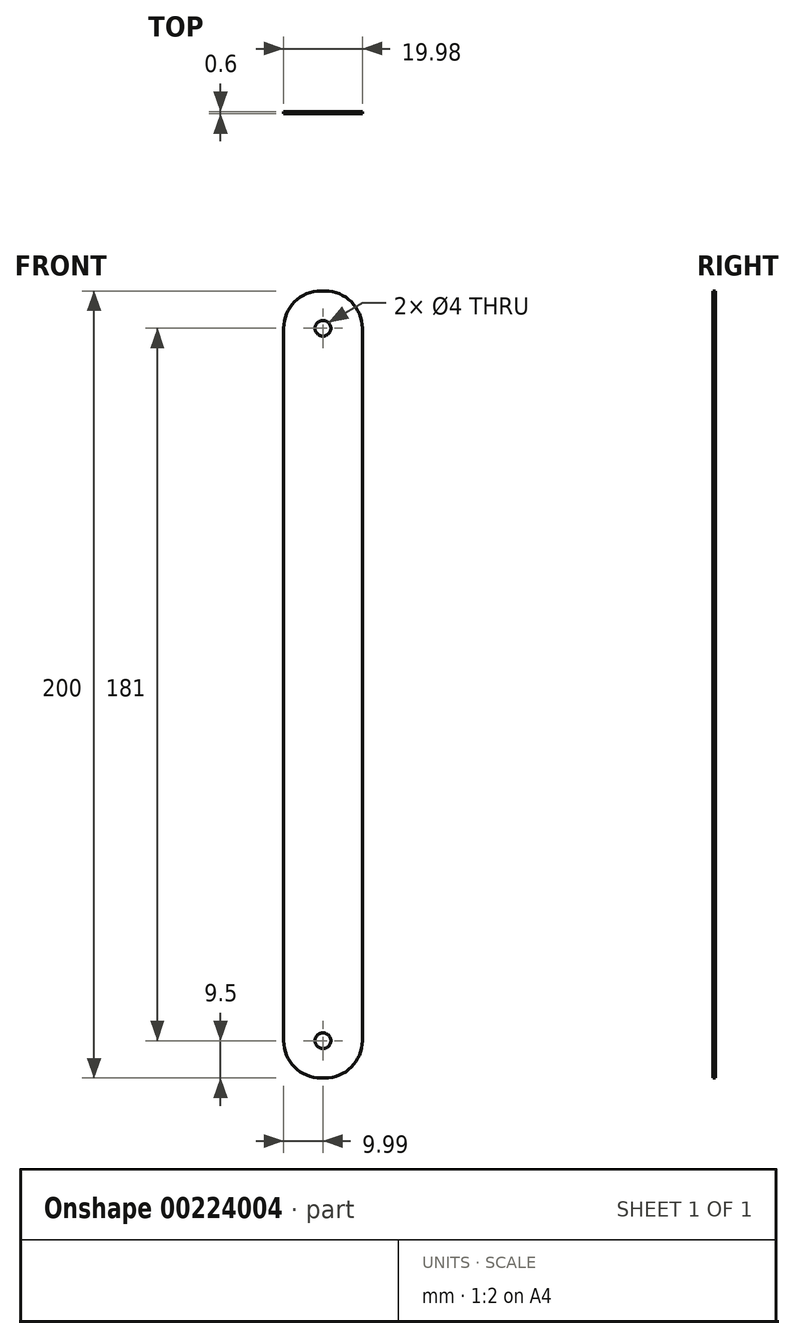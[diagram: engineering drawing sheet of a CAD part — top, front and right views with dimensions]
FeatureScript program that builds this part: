
annotation { "Feature Type Name" : "Feature", "Feature Type Description" : "" }
export const myFeature = defineFeature(function(context is Context, id is Id, definition is map)
    precondition{}
    {
        {
            var Q0;
            Q0=qCreatedBy(makeId("Front.planeOp"),FACE);
            var sketch = newSketch(context, id + "F0", { "sketchPlane" : qUnion([Q0])});
            skLineSegment(sketch, "E0.bottom", {"start": v(-9.98, 100) * mm, "end": v(9.99, 100) * mm});
            skLineSegment(sketch, "E0.top", {"start": v(-9.98, -100) * mm, "end": v(9.99, -100) * mm});
            skLineSegment(sketch, "E0.left", {"start": v(-9.98, 100) * mm, "end": v(-9.99, -100) * mm});
            skLineSegment(sketch, "E0.right", {"start": v(9.99, 100) * mm, "end": v(9.98, -100) * mm});
            skLineSegment(sketch, "E1", {"start": v(-9.98, 0) * mm, "end": v(9.99, 0) * mm});
            skSolve(sketch);
        }
        {
            var Q0;
            Q0 = qSketchRegion(id + "F0", true);
            extrude(context, id + "F1", {"entities" : qUnion([Q0]), "depth" : 0.6 * mm});
        }
        {
            var Q0;
            Q0=makeQuery(id+"F1.opExtrude","SWEPT_EDGE",EDGE,{"disambiguationData":[OSD([sQuery(id+"F0.wireOp",EDGE,"E0.bottom"),sQuery(id+"F0.wireOp",EDGE,"E0.right")])]});
            var Q1;
            Q1=makeQuery(id+"F1.opExtrude","SWEPT_EDGE",EDGE,{"disambiguationData":[OSD([sQuery(id+"F0.wireOp",EDGE,"E0.bottom"),sQuery(id+"F0.wireOp",EDGE,"E0.left")])]});
            var Q2;
            Q2=makeQuery(id+"F1.opExtrude","SWEPT_EDGE",EDGE,{"disambiguationData":[OSD([sQuery(id+"F0.wireOp",EDGE,"E0.top"),sQuery(id+"F0.wireOp",EDGE,"E0.right")])]});
            var Q3;
            Q3=makeQuery(id+"F1.opExtrude","SWEPT_EDGE",EDGE,{"disambiguationData":[OSD([sQuery(id+"F0.wireOp",EDGE,"E0.top"),sQuery(id+"F0.wireOp",EDGE,"E0.left")])]});
            fillet(context, id + "F2", {"entities" : qUnion([Q0, Q1, Q2, Q3]), "radius" : 9.5 * mm, "tangentPropagation" : true, "allowEdgeOverflow" : false});
        }
        {
            var Q0;
            Q0=makeQuery(id+"F1.opExtrude","CAP_FACE",FACE,{"disambiguationData":[OSD([sQuery(id+"F0.wireOp",EDGE,"E0.bottom"),sQuery(id+"F0.wireOp",EDGE,"E0.top"),sQuery(id+"F0.wireOp",EDGE,"E0.left"),sQuery(id+"F0.wireOp",EDGE,"E0.right")])],"isStart":false});
            var sketch = newSketch(context, id + "F3", { "sketchPlane" : qUnion([Q0])});
            skPoint(sketch, "E2.endSnap0", {"position": v(0, 90.5) * mm});
            skCircle(sketch, "E3", {"center": v(0, 90.5) * mm, "radius": 2 * mm});
            skPoint(sketch, "E4.endSnap0", {"position": v(9.99, 0) * mm});
            skCircle(sketch, "E5.MirrorC", {"center": v(0, -90.5) * mm, "radius": 2 * mm});
            skSolve(sketch);
        }
        {
            var Q0;
            Q0 = qSketchRegion(id + "F3", true);
            extrude(context, id + "F4", {"entities" : qUnion([Q0]), "operationType" : NewBodyOperationType.REMOVE, "endBound" : BoundingType.THROUGH_ALL, "oppositeDirection" : true, "depth" : 25 * mm});
        }
    });
